# Revit family: Estrichüberdecktes Kanalsystem EÜK_Vertikalkrümmer_3-zügig
name_source: partatom
category: Generic Models
revit_build: Autodesk Revit 2015 (Build: 20140606_1530(x64)
units: mm (PartAtom-declared; Revit-internal decimal feet)

## types (6) — shared parameters
Manufacturer = OBO Bettermann
Material = Steel, Galvanized
URL = http://www.obo-bettermann.com
Width = 200 mm  [stored 0.656168 ft]

## per-type parameters (varying)
| type | GTIN | Height | Length | Manufacturer Art. No. | Size "a" | Size "b" |
| KV3 25028 | 4012195090403 | 28 mm  [stored 0.0918635 ft] | 250 mm  [stored 0.82021 ft] | 7400644 | 90 mm  [stored 0.295276 ft] | 70 mm  [stored 0.229659 ft] |
| KV3 35028 | 4012195090458 | 28 mm  [stored 0.0918635 ft] | 350 mm  [stored 1.14829 ft] | 7400656 | 120 mm  [stored 0.393701 ft] | 110 mm  [stored 0.360892 ft] |
| KV3 25038 | 4012195090410 | 38 mm  [stored 0.124672 ft] | 250 mm  [stored 0.82021 ft] | 7400648 | 90 mm  [stored 0.295276 ft] | 70 mm  [stored 0.229659 ft] |
| KV3 25048 | 4012195090427 | 48 mm  [stored 0.15748 ft] | 250 mm  [stored 0.82021 ft] | 7400652 | 90 mm  [stored 0.295276 ft] | 70 mm  [stored 0.229659 ft] |
| KV3 35038 | 4012195090465 | 38 mm  [stored 0.124672 ft] | 350 mm  [stored 1.14829 ft] | 7400660 | 120 mm  [stored 0.393701 ft] | 110 mm  [stored 0.360892 ft] |
| KV3 35048 | 4012195090472 | 48 mm  [stored 0.15748 ft] | 350 mm  [stored 1.14829 ft] | 7400664 | 120 mm  [stored 0.393701 ft] | 110 mm  [stored 0.360892 ft] |

note: column(s) folded — value = type name in every type: Article Type

note: [stored X ft] marks values corroborated as IEEE doubles in the binary element streams (Revit-internal decimal feet)

## geometry (parser evidence)
native form markers: Sweep x2
no freeform markers — native parametric forms only
